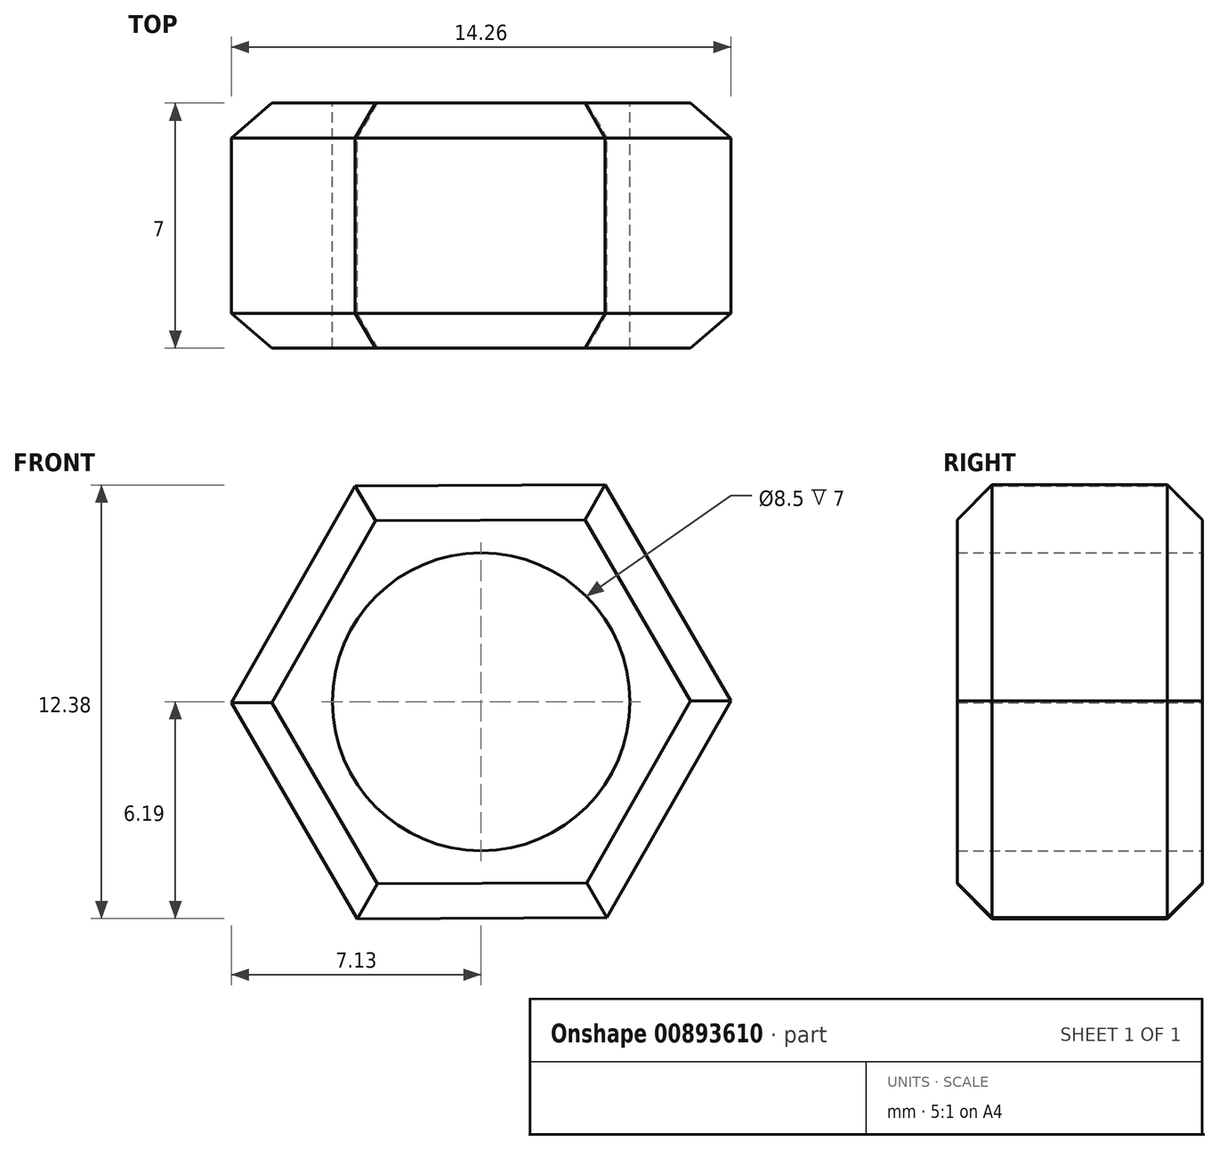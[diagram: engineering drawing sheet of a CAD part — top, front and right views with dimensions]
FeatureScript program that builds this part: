
annotation { "Feature Type Name" : "Feature", "Feature Type Description" : "" }
export const myFeature = defineFeature(function(context is Context, id is Id, definition is map)
    precondition{}
    {
        {
            var Q0;
            Q0=qCreatedBy(makeId("Front.planeOp"),FACE);
            var sketch = newSketch(context, id + "F0", { "sketchPlane" : qUnion([Q0])});
            skCircle(sketch, "E0", {"center": v(0, 0) * mm, "radius": 6.18 * mm});
            skCircle(sketch, "E1.cCircle", {"center": v(0, 0) * mm, "radius": 6.18 * mm, "construction": true});
            skLineSegment(sketch, "E1.0", {"start": v(7.13, 0.03) * mm, "end": v(3.6, -6.16) * mm});
            skLineSegment(sketch, "E1.1", {"start": v(3.6, -6.16) * mm, "end": v(-3.54, -6.2) * mm});
            skLineSegment(sketch, "E1.2", {"start": v(-3.54, -6.2) * mm, "end": v(-7.13, -0.03) * mm});
            skLineSegment(sketch, "E1.3", {"start": v(-7.13, -0.03) * mm, "end": v(-3.6, 6.16) * mm});
            skLineSegment(sketch, "E1.4", {"start": v(-3.6, 6.16) * mm, "end": v(3.54, 6.2) * mm});
            skLineSegment(sketch, "E1.5", {"start": v(3.54, 6.2) * mm, "end": v(7.13, 0.03) * mm});
            skPoint(sketch, "E1.0.midPoint", {"position": v(5.36, -3.07) * mm});
            skSolve(sketch);
        }
        {
            var Q0;
            Q0 = qSketchRegion(id + "F0", true);
            extrude(context, id + "F1", {"entities" : qUnion([Q0]), "depth" : 7 * mm, "offsetDistance" : 25 * mm});
        }
        {
            var Q0;
            Q0=makeQuery(id+"F1.opExtrude","CAP_EDGE",EDGE,{"disambiguationData":[OSD([sQuery(id+"F0.wireOp",EDGE,"E1.3")])],"isStart":false});
            var Q1;
            Q1=makeQuery(id+"F1.opExtrude","CAP_EDGE",EDGE,{"disambiguationData":[OSD([sQuery(id+"F0.wireOp",EDGE,"E1.4")])],"isStart":false});
            var Q2;
            Q2=makeQuery(id+"F1.opExtrude","CAP_EDGE",EDGE,{"disambiguationData":[OSD([sQuery(id+"F0.wireOp",EDGE,"E1.5")])],"isStart":false});
            var Q3;
            Q3=makeQuery(id+"F1.opExtrude","CAP_EDGE",EDGE,{"disambiguationData":[OSD([sQuery(id+"F0.wireOp",EDGE,"E1.0")])],"isStart":false});
            var Q4;
            Q4=makeQuery(id+"F1.opExtrude","CAP_EDGE",EDGE,{"disambiguationData":[OSD([sQuery(id+"F0.wireOp",EDGE,"E1.1")])],"isStart":false});
            var Q5;
            Q5=makeQuery(id+"F1.opExtrude","CAP_EDGE",EDGE,{"disambiguationData":[OSD([sQuery(id+"F0.wireOp",EDGE,"E1.2")])],"isStart":false});
            chamfer(context, id + "F2", {"entities" : qUnion([Q0, Q1, Q2, Q3, Q4, Q5]), "width" : 1 * mm, "tangentPropagation" : true});
        }
        {
            var Q0;
            Q0=makeQuery(id+"F1.opExtrude","CAP_EDGE",EDGE,{"disambiguationData":[OSD([sQuery(id+"F0.wireOp",EDGE,"E1.5")])],"isStart":true});
            var Q1;
            Q1=makeQuery(id+"F1.opExtrude","CAP_EDGE",EDGE,{"disambiguationData":[OSD([sQuery(id+"F0.wireOp",EDGE,"E1.4")])],"isStart":true});
            var Q2;
            Q2=makeQuery(id+"F1.opExtrude","CAP_EDGE",EDGE,{"disambiguationData":[OSD([sQuery(id+"F0.wireOp",EDGE,"E1.3")])],"isStart":true});
            var Q3;
            Q3=makeQuery(id+"F1.opExtrude","CAP_EDGE",EDGE,{"disambiguationData":[OSD([sQuery(id+"F0.wireOp",EDGE,"E1.2")])],"isStart":true});
            var Q4;
            Q4=makeQuery(id+"F1.opExtrude","CAP_EDGE",EDGE,{"disambiguationData":[OSD([sQuery(id+"F0.wireOp",EDGE,"E1.1")])],"isStart":true});
            var Q5;
            Q5=makeQuery(id+"F1.opExtrude","CAP_EDGE",EDGE,{"disambiguationData":[OSD([sQuery(id+"F0.wireOp",EDGE,"E1.0")])],"isStart":true});
            chamfer(context, id + "F3", {"entities" : qUnion([Q0, Q1, Q2, Q3, Q4, Q5]), "width" : 1 * mm, "tangentPropagation" : true});
        }
        {
            var Q0;
            Q0=sQuery(id+"F0.wireOp",VERTEX,"E0.center");
            var Q1;
            Q1=makeQuery(id+"F1.opExtrude","SWEPT_BODY",BODY,{"disambiguationData":[OSD([sQuery(id+"F0.wireOp",EDGE,"E1.0"),sQuery(id+"F0.wireOp",EDGE,"E1.1"),sQuery(id+"F0.wireOp",EDGE,"E1.2"),sQuery(id+"F0.wireOp",EDGE,"E1.3"),sQuery(id+"F0.wireOp",EDGE,"E1.4"),sQuery(id+"F0.wireOp",EDGE,"E1.5")])]});
            hole(context, id + "F4", {"style" : HoleStyle.SIMPLE, "endStyle" : HoleEndStyle.THROUGH, "oppositeDirection" : true, "standardTappedOrClearance" : lookupTablePath({ "standard" : "ISO", "engagement" : "75%", "pitch" : "1.5 mm", "size" : "M10", "type" : "Tapped" }), "standardBlindInLast" : lookupTablePath({ "standard" : "ISO", "engagement" : "75%", "pitch" : "1.5 mm", "size" : "M10", "type" : "Tapped" }), "holeDiameter" : 8.5 * mm, "majorDiameter" : 10 * mm, "showTappedDepth" : true, "isTappedThrough" : true, "tappedDepth" : 12 * mm, "tapClearance" : 3, "locations" : qUnion([Q0]), "scope" : qUnion([Q1])});
        }
    });
